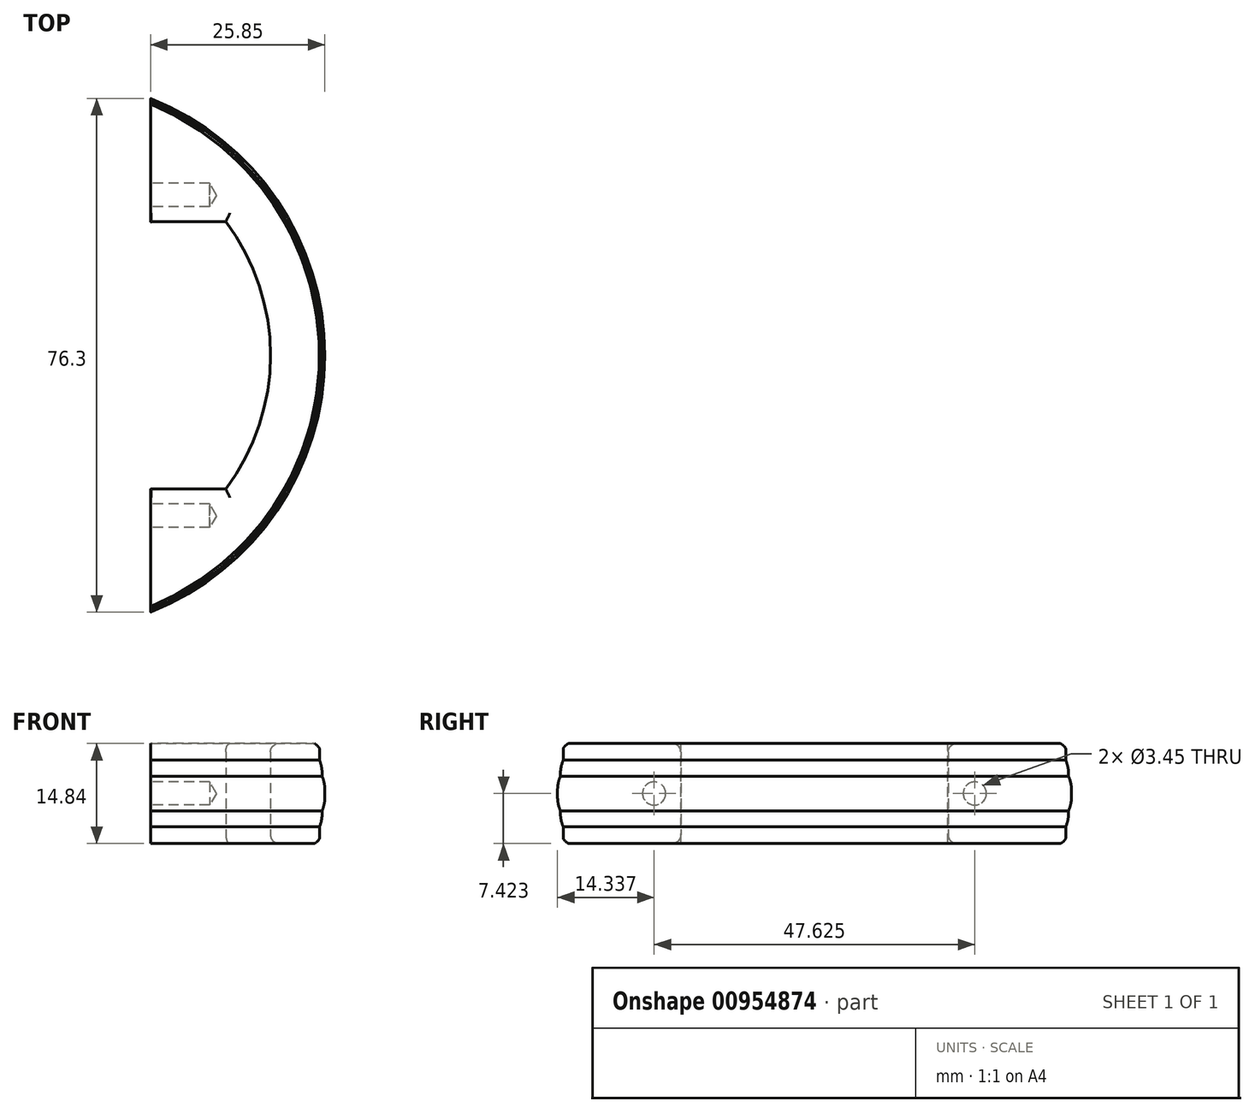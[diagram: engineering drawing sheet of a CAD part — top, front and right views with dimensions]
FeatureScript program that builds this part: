
annotation { "Feature Type Name" : "Feature", "Feature Type Description" : "" }
export const myFeature = defineFeature(function(context is Context, id is Id, definition is map)
    precondition{}
    {
        {
            var Q0;
            Q0=qCreatedBy(makeId("Front.planeOp"),FACE);
            var sketch = newSketch(context, id + "F0", { "sketchPlane" : qUnion([Q0])});
            skLineSegment(sketch, "E0", {"start": v(-55.67, 0) * mm, "end": v(68.03, 0) * mm, "construction": true});
            skLineSegment(sketch, "E1", {"start": v(-7.42, 0) * mm, "end": v(-7.42, 40.28) * mm});
            skLineSegment(sketch, "E2", {"start": v(-7.42, 40.28) * mm, "end": v(-4.96, 40.28) * mm});
            skLineSegment(sketch, "E3", {"start": v(-4.96, 40.28) * mm, "end": v(-4.96, 40.68) * mm});
            skLineSegment(sketch, "E4", {"start": v(-4.96, 40.68) * mm, "end": v(-2.58, 40.68) * mm});
            skLineSegment(sketch, "E5", {"start": v(-2.58, 40.68) * mm, "end": v(-2.58, 41.08) * mm});
            skLineSegment(sketch, "E6", {"start": v(-2.58, 41.08) * mm, "end": v(2.58, 41.08) * mm});
            skLineSegment(sketch, "E7", {"start": v(2.58, 41.08) * mm, "end": v(2.58, 40.68) * mm});
            skLineSegment(sketch, "E8", {"start": v(2.58, 40.68) * mm, "end": v(4.96, 40.68) * mm});
            skLineSegment(sketch, "E9", {"start": v(4.96, 40.68) * mm, "end": v(4.96, 40.28) * mm});
            skLineSegment(sketch, "E10", {"start": v(4.96, 40.28) * mm, "end": v(7.42, 40.28) * mm});
            skLineSegment(sketch, "E11", {"start": v(7.42, 40.28) * mm, "end": v(7.42, 0) * mm});
            skLineSegment(sketch, "E12", {"start": v(7.42, 0) * mm, "end": v(-7.42, 0) * mm});
            skLineSegment(sketch, "E13", {"start": v(0, 0) * mm, "end": v(0, 47.43) * mm, "construction": true});
            skSolve(sketch);
        }
        {
            var Q0;
            Q0=makeQuery(id+"F0.imprint","IMPRINT",FACE,{"disambiguationData":[TD([[makeQuery(id+"F0.imprint","IMPRINT",EDGE,{"derivedFrom":sQuery(id+"F0.wireOp",EDGE,"E1")}),-1.0]])]});
            var Q1;
            Q1=sQuery(id+"F0.wireOp",EDGE,"E0");
            revolve(context, id + "F1", {"surfaceOperationType" : NewSurfaceOperationType.NEW, "entities" : qUnion([Q0]), "axis" : qUnion([Q1]), "revolveType" : RevolveType.FULL});
        }
        {
            var Q0;
            Q0=makeQuery(id+"F1.opRevolve","SWEPT_EDGE",EDGE,{"disambiguationData":[OSD([sQuery(id+"F0.wireOp",EDGE,"E10"),sQuery(id+"F0.wireOp",EDGE,"E11")])]});
            var Q1;
            Q1=makeQuery(id+"F1.opRevolve","SWEPT_EDGE",EDGE,{"disambiguationData":[OSD([sQuery(id+"F0.wireOp",EDGE,"E1"),sQuery(id+"F0.wireOp",EDGE,"E2")])]});
            fillet(context, id + "F2", {"entities" : qUnion([Q0, Q1]), "radius" : 0.76 * mm, "tangentPropagation" : true, "rho" : 0.2, "crossSection" : FilletCrossSection.CONIC, "allowEdgeOverflow" : false});
        }
        {
            var Q0;
            Q0=makeQuery(id+"F1.opRevolve","SWEPT_EDGE",EDGE,{"disambiguationData":[OSD([sQuery(id+"F0.wireOp",EDGE,"E8"),sQuery(id+"F0.wireOp",EDGE,"E9")])]});
            var Q1;
            Q1=makeQuery(id+"F1.opRevolve","SWEPT_EDGE",EDGE,{"disambiguationData":[OSD([sQuery(id+"F0.wireOp",EDGE,"E3"),sQuery(id+"F0.wireOp",EDGE,"E4")])]});
            fillet(context, id + "F3", {"entities" : qUnion([Q0, Q1]), "radius" : 5.08 * mm, "tangentPropagation" : true, "allowEdgeOverflow" : false});
        }
        {
            var Q0;
            Q0=makeQuery(id+"F1.opRevolve","SWEPT_EDGE",EDGE,{"disambiguationData":[OSD([sQuery(id+"F0.wireOp",EDGE,"E6"),sQuery(id+"F0.wireOp",EDGE,"E7")])]});
            var Q1;
            Q1=makeQuery(id+"F1.opRevolve","SWEPT_EDGE",EDGE,{"disambiguationData":[OSD([sQuery(id+"F0.wireOp",EDGE,"E5"),sQuery(id+"F0.wireOp",EDGE,"E6")])]});
            fillet(context, id + "F4", {"entities" : qUnion([Q0, Q1]), "radius" : 5.08 * mm, "tangentPropagation" : true, "allowEdgeOverflow" : false});
        }
        {
            var Q0;
            Q0=qCreatedBy(makeId("Right.planeOp"),FACE);
            var sketch = newSketch(context, id + "F5", { "sketchPlane" : qUnion([Q0])});
            skCircle(sketch, "E14", {"center": v(0, 0) * mm, "radius": 25 * mm});
            skSolve(sketch);
        }
        {
            var Q0;
            Q0=qSketchRegion(id+"F5",true);
            extrude(context, id + "F6", {"entities" : qUnion([Q0]), "operationType" : NewBodyOperationType.REMOVE, "endBound" : BoundingType.THROUGH_ALL, "depth" : 25.4 * mm, "offsetDistance" : 25.4 * mm, "hasSecondDirection" : true, "secondDirectionBound" : SecondDirectionBoundingType.THROUGH_ALL, "secondDirectionOppositeDirection" : true, "secondDirectionDepth" : 25.4 * mm});
        }
        {
            var Q0;
            Q0=qCreatedBy(makeId("Right.planeOp"),FACE);
            var sketch = newSketch(context, id + "F7", { "sketchPlane" : qUnion([Q0])});
            skLineSegment(sketch, "E15", {"start": v(0, 15.23) * mm, "end": v(-38.1, 15.23) * mm, "construction": true});
            skLineSegment(sketch, "E16.MirrorCS", {"start": v(0, 15.23) * mm, "end": v(38.1, 15.23) * mm, "construction": true});
            skLineSegment(sketch, "E17", {"start": v(-59.25, 15.23) * mm, "end": v(65.7, 15.23) * mm});
            skLineSegment(sketch, "E18", {"start": v(65.7, 15.23) * mm, "end": v(65.7, -43.9) * mm});
            skLineSegment(sketch, "E19", {"start": v(65.7, -43.9) * mm, "end": v(-59.25, -43.9) * mm});
            skLineSegment(sketch, "E20", {"start": v(-59.25, -43.9) * mm, "end": v(-59.25, 15.23) * mm});
            skSolve(sketch);
        }
        {
            var Q0;
            Q0=qSketchRegion(id+"F7",true);
            extrude(context, id + "F8", {"entities" : qUnion([Q0]), "operationType" : NewBodyOperationType.REMOVE, "endBound" : BoundingType.THROUGH_ALL, "oppositeDirection" : true, "depth" : 25.4 * mm, "offsetDistance" : 25.4 * mm, "hasSecondDirection" : true, "secondDirectionBound" : SecondDirectionBoundingType.THROUGH_ALL, "secondDirectionOppositeDirection" : false, "secondDirectionDepth" : 25.4 * mm});
        }
        {
            var Q0;
            Q0=qCreatedBy(makeId("Right.planeOp"),FACE);
            var sketch = newSketch(context, id + "F9", { "sketchPlane" : qUnion([Q0])});
            skLineSegment(sketch, "E21", {"start": v(-19.86, 15.26) * mm, "end": v(-19.86, 26.38) * mm});
            skLineSegment(sketch, "E22.MirrorCS", {"start": v(19.86, 15.26) * mm, "end": v(19.86, 26.38) * mm});
            skArc(sketch, "E23", {"start": v(-19.86, 26.38) * mm, "mid": v(0, 33.01) * mm, "end": v(19.86, 26.38) * mm});
            skLineSegment(sketch, "E24", {"start": v(-19.86, 15.26) * mm, "end": v(19.86, 15.26) * mm});
            skSolve(sketch);
        }
        {
            var Q0;
            Q0=qSketchRegion(id+"F9",true);
            extrude(context, id + "F10", {"entities" : qUnion([Q0]), "operationType" : NewBodyOperationType.REMOVE, "endBound" : BoundingType.THROUGH_ALL, "oppositeDirection" : true, "depth" : 25.4 * mm, "offsetDistance" : 25.4 * mm, "hasSecondDirection" : true, "secondDirectionBound" : SecondDirectionBoundingType.THROUGH_ALL, "secondDirectionOppositeDirection" : false, "secondDirectionDepth" : 25.4 * mm});
        }
        {
            var Q0;
            Q0=makeQuery(id+"F10.boolean.opBoolean","INTERSECT",EDGE,{"derivedFrom":[makeQuery(id+"F1.opRevolve","SWEPT_FACE",FACE,{"disambiguationData":[OSD([sQuery(id+"F0.wireOp",EDGE,"E11")])]}),makeQuery(id+"F10.opExtrude","SWEPT_FACE",FACE,{"disambiguationData":[OSD([sQuery(id+"F9.wireOp",EDGE,"E23")])]})]});
            var Q1;
            Q1=makeQuery(id+"F10.boolean.opBoolean","INTERSECT",EDGE,{"derivedFrom":[makeQuery(id+"F1.opRevolve","SWEPT_FACE",FACE,{"disambiguationData":[OSD([sQuery(id+"F0.wireOp",EDGE,"E11")])]}),makeQuery(id+"F10.opExtrude","SWEPT_FACE",FACE,{"disambiguationData":[OSD([sQuery(id+"F9.wireOp",EDGE,"E21")])]})]});
            var Q2;
            Q2=makeQuery(id+"F10.boolean.opBoolean","INTERSECT",EDGE,{"derivedFrom":[makeQuery(id+"F1.opRevolve","SWEPT_FACE",FACE,{"disambiguationData":[OSD([sQuery(id+"F0.wireOp",EDGE,"E11")])]}),makeQuery(id+"F10.opExtrude","SWEPT_FACE",FACE,{"disambiguationData":[OSD([sQuery(id+"F9.wireOp",EDGE,"E22.MirrorCS")])]})]});
            var Q3;
            Q3=makeQuery(id+"F10.boolean.opBoolean","INTERSECT",EDGE,{"derivedFrom":[makeQuery(id+"F1.opRevolve","SWEPT_FACE",FACE,{"disambiguationData":[OSD([sQuery(id+"F0.wireOp",EDGE,"E1")])]}),makeQuery(id+"F10.opExtrude","SWEPT_FACE",FACE,{"disambiguationData":[OSD([sQuery(id+"F9.wireOp",EDGE,"E23")])]})]});
            var Q4;
            Q4=makeQuery(id+"F10.boolean.opBoolean","INTERSECT",EDGE,{"derivedFrom":[makeQuery(id+"F1.opRevolve","SWEPT_FACE",FACE,{"disambiguationData":[OSD([sQuery(id+"F0.wireOp",EDGE,"E1")])]}),makeQuery(id+"F10.opExtrude","SWEPT_FACE",FACE,{"disambiguationData":[OSD([sQuery(id+"F9.wireOp",EDGE,"E21")])]})]});
            var Q5;
            Q5=makeQuery(id+"F10.boolean.opBoolean","INTERSECT",EDGE,{"derivedFrom":[makeQuery(id+"F1.opRevolve","SWEPT_FACE",FACE,{"disambiguationData":[OSD([sQuery(id+"F0.wireOp",EDGE,"E1")])]}),makeQuery(id+"F10.opExtrude","SWEPT_FACE",FACE,{"disambiguationData":[OSD([sQuery(id+"F9.wireOp",EDGE,"E22.MirrorCS")])]})]});
            fillet(context, id + "F11", {"entities" : qUnion([Q0, Q1, Q2, Q3, Q4, Q5]), "radius" : 1.27 * mm, "tangentPropagation" : true, "allowEdgeOverflow" : false});
        }
        {
            var Q0;
            Q0=qCreatedBy(makeId("Top.planeOp"),FACE);
            var sketch = newSketch(context, id + "F12", { "sketchPlane" : qUnion([Q0])});
            skLineSegment(sketch, "E25", {"start": v(-14.34, 23.81) * mm, "end": v(15.86, 23.81) * mm, "construction": true});
            skLineSegment(sketch, "E26.MirrorCS", {"start": v(-14.34, -23.81) * mm, "end": v(15.86, -23.81) * mm, "construction": true});
            skPoint(sketch, "E27", {"position": v(0, 23.81) * mm});
            skPoint(sketch, "E28", {"position": v(0, -23.81) * mm});
            skSolve(sketch);
        }
        {
            var Q0;
            Q0=sQuery(id+"F12.wireOp",VERTEX,"E28");
            var Q1;
            Q1=sQuery(id+"F12.wireOp",VERTEX,"E27");
            var Q2;
            Q2=makeQuery(id+"F1.opRevolve","SWEPT_BODY",BODY,{"disambiguationData":[OSD([sQuery(id+"F0.wireOp",EDGE,"E1"),sQuery(id+"F0.wireOp",EDGE,"E2"),sQuery(id+"F0.wireOp",EDGE,"E3"),sQuery(id+"F0.wireOp",EDGE,"E4"),sQuery(id+"F0.wireOp",EDGE,"E5"),sQuery(id+"F0.wireOp",EDGE,"E6"),sQuery(id+"F0.wireOp",EDGE,"E7"),sQuery(id+"F0.wireOp",EDGE,"E8"),sQuery(id+"F0.wireOp",EDGE,"E9"),sQuery(id+"F0.wireOp",EDGE,"E10"),sQuery(id+"F0.wireOp",EDGE,"E11"),sQuery(id+"F0.wireOp",EDGE,"E12")])]});
            hole(context, id + "F13", {"style" : HoleStyle.SIMPLE, "endStyle" : HoleEndStyle.BLIND, "oppositeDirection" : true, "standardTappedOrClearance" : lookupTablePath({ "standard" : "ANSI", "engagement" : "75%", "pitch" : "32 tpi", "size" : "#8", "type" : "Tapped" }), "standardBlindInLast" : lookupTablePath({ "standard" : "ANSI", "fit" : "Normal", "engagement" : "75%", "pitch" : "32 tpi", "size" : "#8", "type" : "Clearance & tapped" }), "holeDiameter" : 3.45 * mm, "majorDiameter" : 4.17 * mm, "showTappedDepth" : true, "holeDepth" : 23.97 * mm, "isTappedThrough" : true, "tappedDepth" : 21.59 * mm, "tapClearance" : 3, "startFromSketch" : true, "locations" : qUnion([Q0, Q1]), "scope" : qUnion([Q2])});
        }
        {
            var Q0;
            Q0=makeQuery(id+"F1.opRevolve","SWEPT_BODY",BODY,{"disambiguationData":[OSD([sQuery(id+"F0.wireOp",EDGE,"E1"),sQuery(id+"F0.wireOp",EDGE,"E2"),sQuery(id+"F0.wireOp",EDGE,"E3"),sQuery(id+"F0.wireOp",EDGE,"E4"),sQuery(id+"F0.wireOp",EDGE,"E5"),sQuery(id+"F0.wireOp",EDGE,"E6"),sQuery(id+"F0.wireOp",EDGE,"E7"),sQuery(id+"F0.wireOp",EDGE,"E8"),sQuery(id+"F0.wireOp",EDGE,"E9"),sQuery(id+"F0.wireOp",EDGE,"E10"),sQuery(id+"F0.wireOp",EDGE,"E11"),sQuery(id+"F0.wireOp",EDGE,"E12")])]});
            var Q1;
            Q1=makeQuery(id+"F8.boolean.opBoolean","INTERSECT",EDGE,{"disambiguationData":[OD(1.0)],"derivedFrom":[makeQuery(id+"F1.opRevolve","SWEPT_FACE",FACE,{"disambiguationData":[OSD([sQuery(id+"F0.wireOp",EDGE,"E11")])]}),makeQuery(id+"F8.opExtrude","SWEPT_FACE",FACE,{"disambiguationData":[OSD([sQuery(id+"F7.wireOp",EDGE,"E17")])]})]});
            transform(context, id + "F14", {"entities" : qUnion([Q0]), "transformType" : TransformType.ROTATION, "transformAxis" : qUnion([Q1]), "angle" : 90 * degree, "makeCopy" : false});
        }
    });
